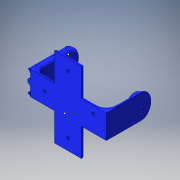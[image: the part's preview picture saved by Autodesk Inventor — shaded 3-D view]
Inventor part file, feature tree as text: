
AUTODESK INVENTOR PART (.ipt)
format: ipt  version: 2016 (Build 200138000, 138)  size: 570,368 bytes
history: native  units: in
note: dims shown in document units (in); Inventor stores cm internally (conversion verified against a paired STEP export)
features: sketch x13, other x3
ambient origin geometry x8: Origin, YZ Plane, XZ Plane, XY Plane, X Axis, Y Axis, Z Axis, Center Point
bodies: Solid1 (feature_tree)
feature tree (16):
  other  "Hip_forward_v2.ipt"
  other  "Solid1::Hip_forward_v2.ipt"
  other  "TaggingFeature1"
  sketch  "Sketch1"  dims[d0=0.3937in]
  sketch  "Sketch4"
  sketch  "Sketch5"
  sketch  "Sketch7"
  sketch  "Sketch9"
  sketch  "Sketch10"
  sketch  "Sketch15"
  sketch  "Sketch16"
  sketch  "Sketch17"
  sketch  "Sketch18"
  sketch  "Sketch19"
  sketch  "Sketch20"
  sketch  "Sketch21"
